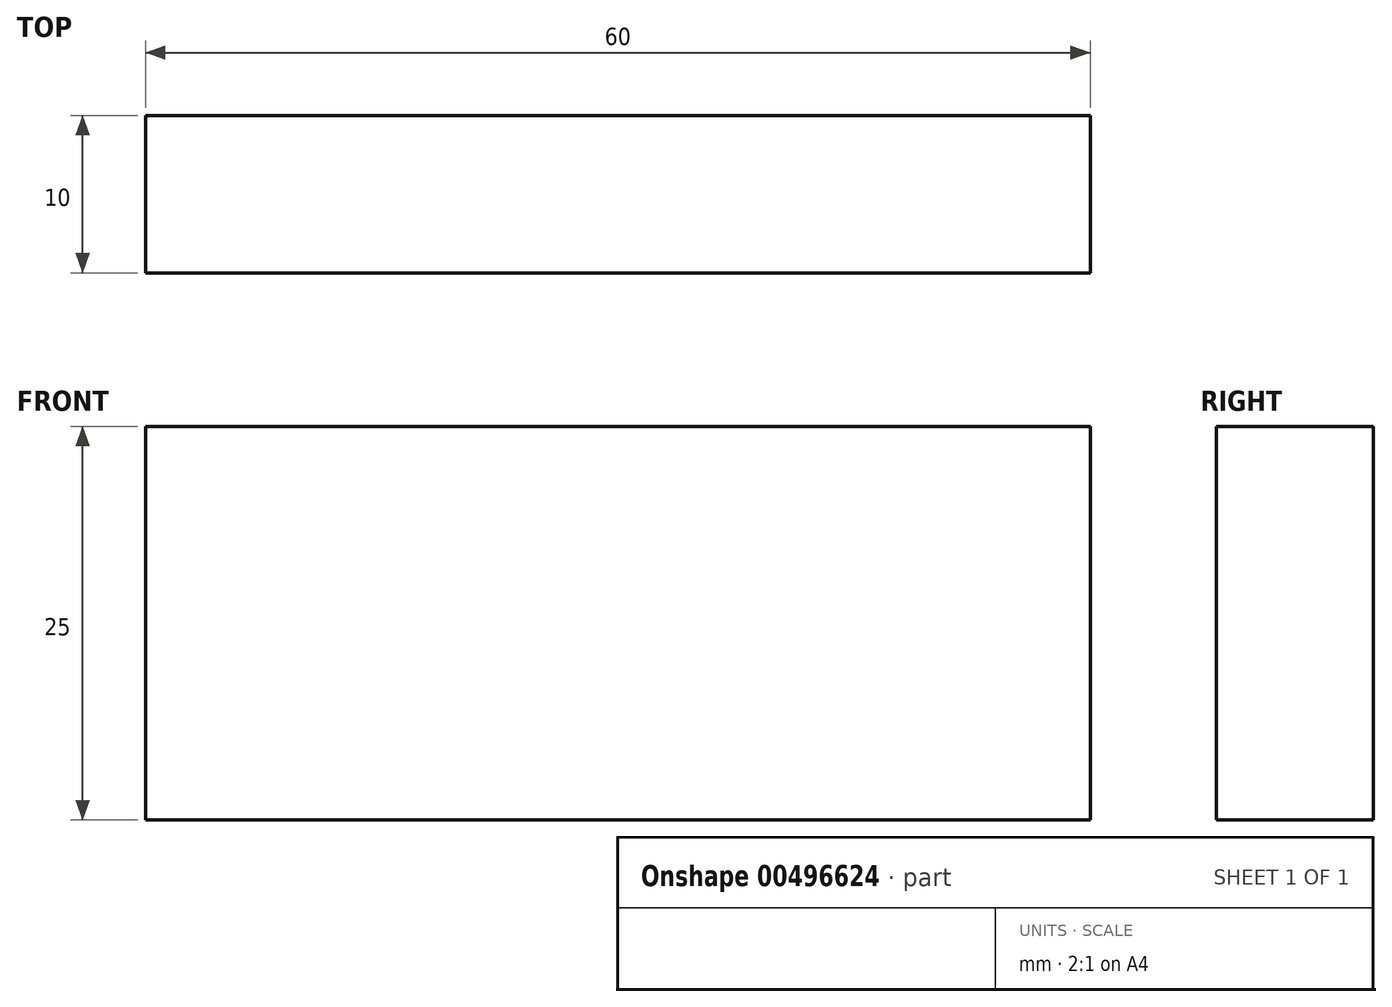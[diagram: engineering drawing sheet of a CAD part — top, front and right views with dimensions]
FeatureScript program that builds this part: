
annotation { "Feature Type Name" : "Feature", "Feature Type Description" : "" }
export const myFeature = defineFeature(function(context is Context, id is Id, definition is map)
    precondition{}
    {
        {
            var Q0;
            Q0=qCreatedBy(makeId("Top.planeOp"),FACE);
            var sketch = newSketch(context, id + "F0", { "sketchPlane" : qUnion([Q0])});
            skLineSegment(sketch, "E0", {"start": v(0, 0) * mm, "end": v(-60, 0) * mm});
            skLineSegment(sketch, "E1", {"start": v(-60, 0) * mm, "end": v(-60, 10) * mm});
            skLineSegment(sketch, "E2", {"start": v(0, 0) * mm, "end": v(0, 10) * mm});
            skLineSegment(sketch, "E3", {"start": v(-60, 10) * mm, "end": v(0, 10) * mm});
            skSolve(sketch);
        }
        {
            var Q0;
            Q0=makeQuery(id+"F0.imprint","IMPRINT",FACE,{"disambiguationData":[TD([[makeQuery(id+"F0.imprint","IMPRINT",EDGE,{"derivedFrom":sQuery(id+"F0.wireOp",EDGE,"E0")}),-1.0]])]});
            extrude(context, id + "F1", {"entities" : qUnion([Q0]), "depth" : 25 * mm});
        }
    });
